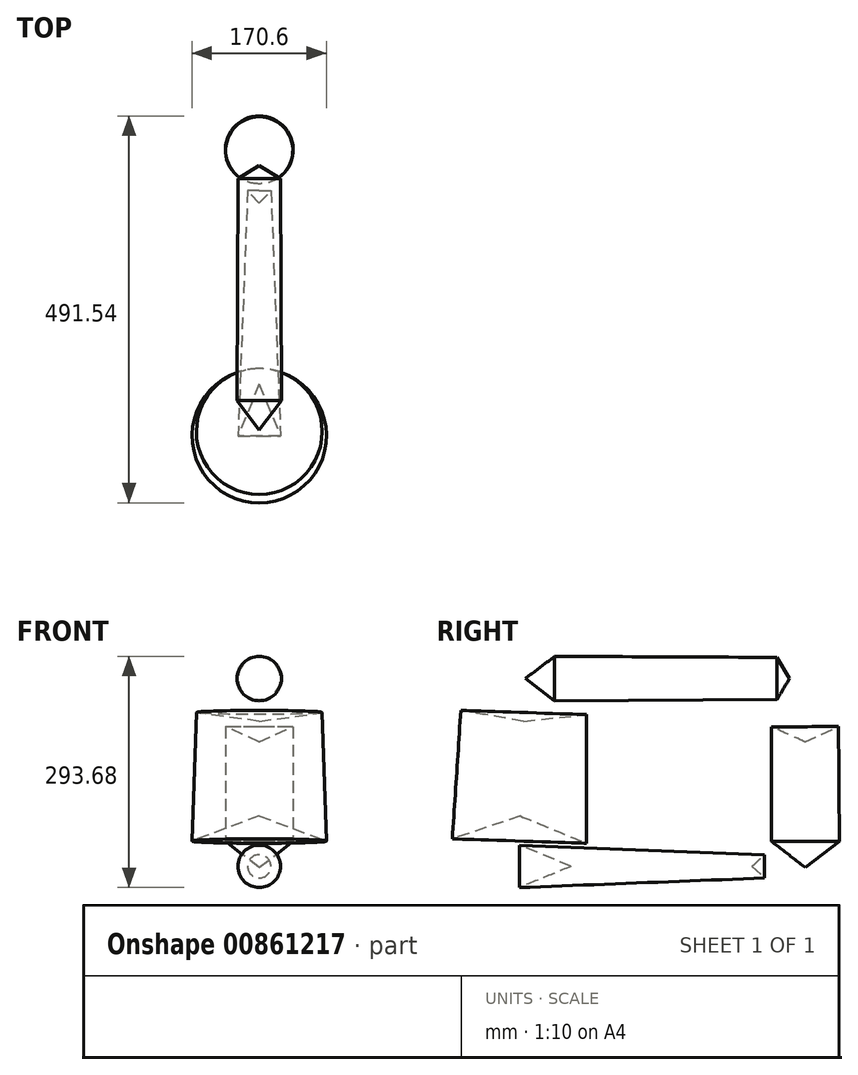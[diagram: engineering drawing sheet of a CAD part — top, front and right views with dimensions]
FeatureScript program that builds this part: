
annotation { "Feature Type Name" : "Feature", "Feature Type Description" : "" }
export const myFeature = defineFeature(function(context is Context, id is Id, definition is map)
    precondition{}
    {
        {
            var Q0;
            Q0=qCreatedBy(makeId("Right.planeOp"),FACE);
            var sketch = newSketch(context, id + "F0", { "sketchPlane" : qUnion([Q0])});
            skLineSegment(sketch, "E0", {"start": v(-120.43, 74.17) * mm, "end": v(-200.67, 65.75) * mm});
            skLineSegment(sketch, "E1", {"start": v(-200.67, 65.75) * mm, "end": v(-204.64, -54.72) * mm});
            skLineSegment(sketch, "E2", {"start": v(-120.43, 74.17) * mm, "end": v(-120.43, -89.32) * mm});
            skLineSegment(sketch, "E3", {"start": v(-120.43, -89.32) * mm, "end": v(-204.64, -54.72) * mm});
            skLineSegment(sketch, "E4", {"start": v(157.05, 39.4) * mm, "end": v(114.35, 58.64) * mm});
            skLineSegment(sketch, "E5", {"start": v(114.35, 58.64) * mm, "end": v(114.35, -86.96) * mm});
            skLineSegment(sketch, "E6", {"start": v(114.35, -86.96) * mm, "end": v(157.59, -120.23) * mm});
            skLineSegment(sketch, "E7", {"start": v(157.59, -120.23) * mm, "end": v(157.05, 39.4) * mm});
            skLineSegment(sketch, "E8", {"start": v(121.22, 93.1) * mm, "end": v(137.35, 119.95) * mm});
            skLineSegment(sketch, "E9", {"start": v(137.35, 119.95) * mm, "end": v(-198.3, 119.95) * mm});
            skLineSegment(sketch, "E10", {"start": v(-198.3, 119.95) * mm, "end": v(-161.01, 91.79) * mm});
            skLineSegment(sketch, "E11", {"start": v(-161.01, 91.79) * mm, "end": v(121.22, 93.1) * mm});
            skLineSegment(sketch, "E12", {"start": v(105.62, -103.8) * mm, "end": v(-205.83, -91.71) * mm});
            skLineSegment(sketch, "E13", {"start": v(-205.83, -91.71) * mm, "end": v(-140.13, -118.65) * mm});
            skLineSegment(sketch, "E14", {"start": v(-140.13, -118.65) * mm, "end": v(89.76, -118.65) * mm});
            skLineSegment(sketch, "E15", {"start": v(89.76, -118.65) * mm, "end": v(105.62, -103.8) * mm});
            skSolve(sketch);
        }
        {
            var Q0;
            Q0=makeQuery(id+"F0.imprint","IMPRINT",FACE,{"disambiguationData":[TD([[makeQuery(id+"F0.imprint","IMPRINT",EDGE,{"derivedFrom":sQuery(id+"F0.wireOp",EDGE,"E8")}),1.0]])]});
            var Q1;
            Q1=sQuery(id+"F0.wireOp",EDGE,"E9");
            revolve(context, id + "F1", {"surfaceOperationType" : NewSurfaceOperationType.NEW, "entities" : qUnion([Q0]), "axis" : qUnion([Q1]), "revolveType" : RevolveType.FULL});
        }
        {
            var Q0;
            Q0=makeQuery(id+"F0.imprint","IMPRINT",FACE,{"disambiguationData":[TD([[makeQuery(id+"F0.imprint","IMPRINT",EDGE,{"derivedFrom":sQuery(id+"F0.wireOp",EDGE,"E0")}),1.0]])]});
            var Q1;
            Q1=sQuery(id+"F0.wireOp",EDGE,"E1");
            revolve(context, id + "F2", {"surfaceOperationType" : NewSurfaceOperationType.NEW, "entities" : qUnion([Q0]), "axis" : qUnion([Q1]), "revolveType" : RevolveType.FULL});
        }
        {
            var Q0;
            Q0=makeQuery(id+"F0.imprint","IMPRINT",FACE,{"disambiguationData":[TD([[makeQuery(id+"F0.imprint","IMPRINT",EDGE,{"derivedFrom":sQuery(id+"F0.wireOp",EDGE,"E12")}),1.0]])]});
            var Q1;
            Q1=sQuery(id+"F0.wireOp",EDGE,"E14");
            revolve(context, id + "F3", {"surfaceOperationType" : NewSurfaceOperationType.NEW, "entities" : qUnion([Q0]), "axis" : qUnion([Q1]), "revolveType" : RevolveType.FULL});
        }
        {
            var Q0;
            Q0=makeQuery(id+"F0.imprint","IMPRINT",FACE,{"disambiguationData":[TD([[makeQuery(id+"F0.imprint","IMPRINT",EDGE,{"derivedFrom":sQuery(id+"F0.wireOp",EDGE,"E4")}),1.0]])]});
            var Q1;
            Q1=sQuery(id+"F0.wireOp",EDGE,"E7");
            revolve(context, id + "F4", {"surfaceOperationType" : NewSurfaceOperationType.NEW, "entities" : qUnion([Q0]), "axis" : qUnion([Q1]), "revolveType" : RevolveType.FULL});
        }
    });
